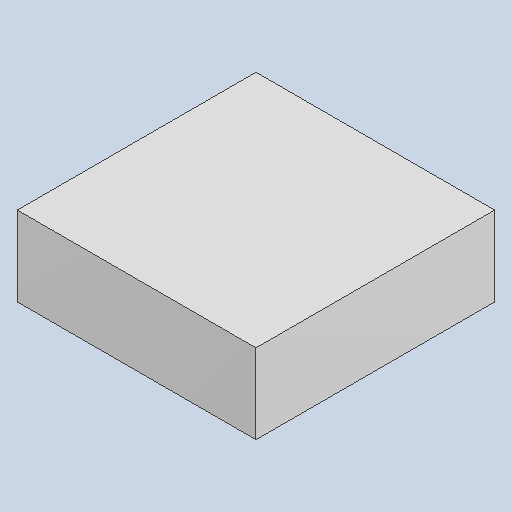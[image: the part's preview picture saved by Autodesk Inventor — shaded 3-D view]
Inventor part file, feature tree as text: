
AUTODESK INVENTOR PART (.ipt)
format: ipt  version: 2023.4 (Build 274418000, 418)  size: 79,872 bytes
history: native  units: mm
features: extrude x1
ambient origin geometry x8: Origin, YZ Plane, XZ Plane, XY Plane, X Axis, Y Axis, Z Axis, Center Point
bodies: Solid1 (feature_tree)
feature tree (1):
  extrude  "Extruded_51"  [1 undecoded]
note: 1 required parameter value undecoded (feature->parameter linkage not recoverable at this tier; creation-order binding heuristic only, values carry confidence <= 0.55)
